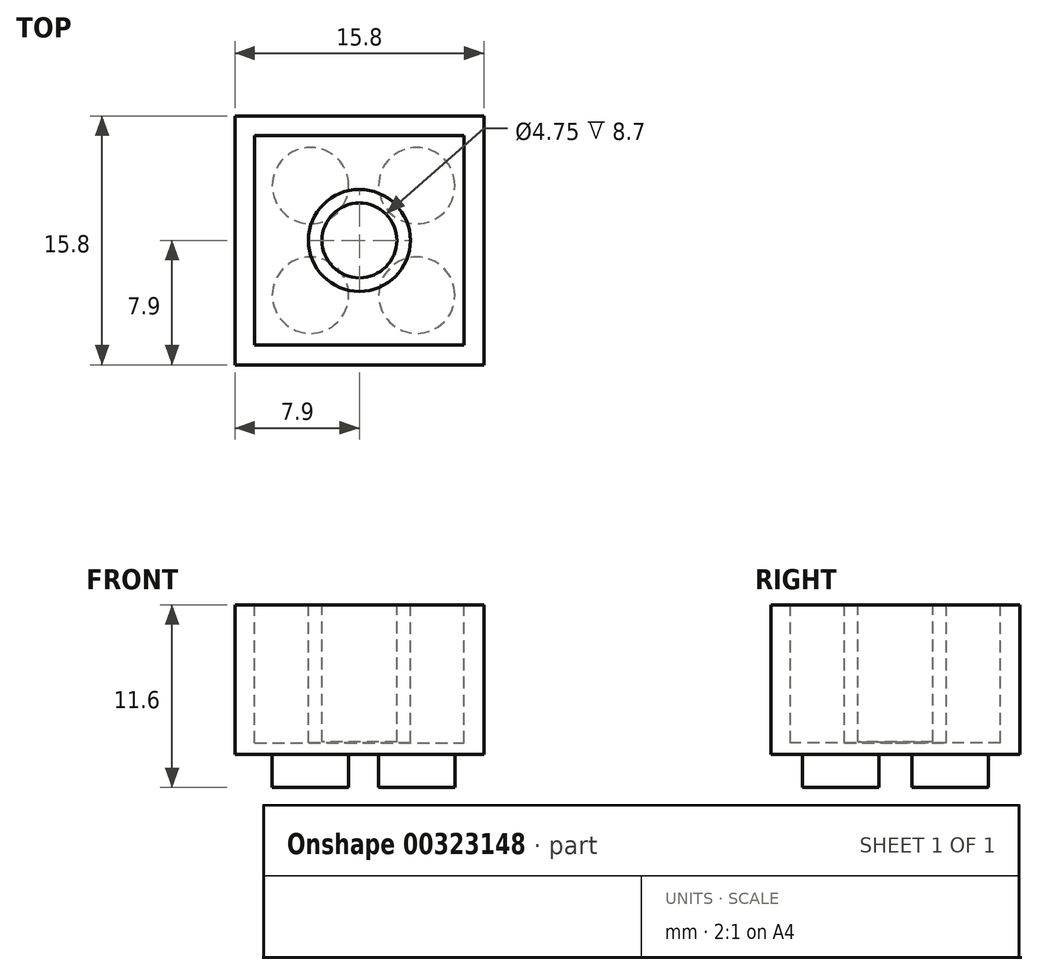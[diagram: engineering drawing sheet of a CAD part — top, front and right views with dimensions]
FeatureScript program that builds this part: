
annotation { "Feature Type Name" : "Feature", "Feature Type Description" : "" }
export const myFeature = defineFeature(function(context is Context, id is Id, definition is map)
    precondition{}
    {
        {
            var Q0;
            Q0=qCreatedBy(makeId("Top.planeOp"),FACE);
            var sketch = newSketch(context, id + "F0", { "sketchPlane" : qUnion([Q0])});
            skLineSegment(sketch, "E0.bottom", {"start": v(7.9, -7.9) * mm, "end": v(-7.9, -7.9) * mm});
            skLineSegment(sketch, "E0.top", {"start": v(7.9, 7.9) * mm, "end": v(-7.9, 7.9) * mm});
            skLineSegment(sketch, "E0.left", {"start": v(7.9, -7.9) * mm, "end": v(7.9, 7.9) * mm});
            skLineSegment(sketch, "E0.right", {"start": v(-7.9, -7.9) * mm, "end": v(-7.9, 7.9) * mm});
            skPoint(sketch, "E0.middle", {"position": v(0, 0) * mm});
            skCircle(sketch, "E1", {"center": v(-3.1, 3.48) * mm, "radius": 2.43 * mm});
            skCircle(sketch, "E2", {"center": v(-3.1, -3.48) * mm, "radius": 2.43 * mm});
            skCircle(sketch, "E3", {"center": v(3.64, -3.48) * mm, "radius": 2.43 * mm});
            skCircle(sketch, "E4", {"center": v(3.64, 3.48) * mm, "radius": 2.43 * mm});
            skSolve(sketch);
        }
        {
            var Q0;
            Q0=makeQuery(id+"F0.imprint","IMPRINT",FACE,{"disambiguationData":[TD([[makeQuery(id+"F0.imprint","IMPRINT",EDGE,{"derivedFrom":sQuery(id+"F0.wireOp",EDGE,"E0.bottom")}),-1.0]])]});
            var Q1;
            Q1=makeQuery(id+"F0.imprint","IMPRINT",FACE,{"disambiguationData":[TD([[makeQuery(id+"F0.imprint","IMPRINT",EDGE,{"derivedFrom":sQuery(id+"F0.wireOp",EDGE,"4mF0htgy-tboj-X3VI-CUVx-4Nb7YP2AiGV2")}),1.0]])]});
            var Q2;
            Q2=makeQuery(id+"F0.imprint","IMPRINT",FACE,{"disambiguationData":[TD([[makeQuery(id+"F0.imprint","IMPRINT",EDGE,{"derivedFrom":sQuery(id+"F0.wireOp",EDGE,"E3")}),1.0]])]});
            var Q3;
            Q3=makeQuery(id+"F0.imprint","IMPRINT",FACE,{"disambiguationData":[TD([[makeQuery(id+"F0.imprint","IMPRINT",EDGE,{"derivedFrom":sQuery(id+"F0.wireOp",EDGE,"E2")}),1.0]])]});
            var Q4;
            Q4=makeQuery(id+"F0.imprint","IMPRINT",FACE,{"disambiguationData":[TD([[makeQuery(id+"F0.imprint","IMPRINT",EDGE,{"derivedFrom":sQuery(id+"F0.wireOp",EDGE,"E1")}),1.0]])]});
            var Q5;
            Q5=makeQuery(id+"F0.imprint","IMPRINT",FACE,{"disambiguationData":[TD([[makeQuery(id+"F0.imprint","IMPRINT",EDGE,{"derivedFrom":sQuery(id+"F0.wireOp",EDGE,"E4")}),1.0]])]});
            extrude(context, id + "F1", {"entities" : qUnion([Q0, Q1, Q2, Q3, Q4, Q5]), "depth" : 9.5 * mm});
        }
        {
            var Q0;
            Q0=makeQuery(id+"F0.imprint","IMPRINT",FACE,{"disambiguationData":[TD([[makeQuery(id+"F0.imprint","IMPRINT",EDGE,{"derivedFrom":sQuery(id+"F0.wireOp",EDGE,"E4")}),1.0]])]});
            var Q1;
            Q1=makeQuery(id+"F0.imprint","IMPRINT",FACE,{"disambiguationData":[TD([[makeQuery(id+"F0.imprint","IMPRINT",EDGE,{"derivedFrom":sQuery(id+"F0.wireOp",EDGE,"E1")}),1.0]])]});
            var Q2;
            Q2=makeQuery(id+"F0.imprint","IMPRINT",FACE,{"disambiguationData":[TD([[makeQuery(id+"F0.imprint","IMPRINT",EDGE,{"derivedFrom":sQuery(id+"F0.wireOp",EDGE,"E2")}),1.0]])]});
            var Q3;
            Q3=makeQuery(id+"F0.imprint","IMPRINT",FACE,{"disambiguationData":[TD([[makeQuery(id+"F0.imprint","IMPRINT",EDGE,{"derivedFrom":sQuery(id+"F0.wireOp",EDGE,"E3")}),1.0]])]});
            extrude(context, id + "F2", {"entities" : qUnion([Q0, Q1, Q2, Q3]), "operationType" : NewBodyOperationType.ADD, "oppositeDirection" : true, "depth" : 2.1 * mm});
        }
        {
            var Q0;
            Q0=makeQuery(id+"F1.opExtrude","CAP_FACE",FACE,{"disambiguationData":[OSD([sQuery(id+"F0.wireOp",EDGE,"E0.bottom"),sQuery(id+"F0.wireOp",EDGE,"E0.top"),sQuery(id+"F0.wireOp",EDGE,"E0.left"),sQuery(id+"F0.wireOp",EDGE,"E0.right")])],"isStart":false});
            var sketch = newSketch(context, id + "F3", { "sketchPlane" : qUnion([Q0])});
            skCircle(sketch, "E5", {"center": v(0, 0) * mm, "radius": 3.24 * mm});
            skLineSegment(sketch, "E6.bottom", {"start": v(-7.9, 7.9) * mm, "end": v(-6.66, 7.9) * mm});
            skLineSegment(sketch, "E6.top", {"start": v(-7.9, -7.9) * mm, "end": v(-6.66, -7.9) * mm});
            skLineSegment(sketch, "E6.left", {"start": v(-7.9, 7.9) * mm, "end": v(-7.9, -7.9) * mm});
            skLineSegment(sketch, "E6.right", {"start": v(-6.66, 7.9) * mm, "end": v(-6.66, -7.9) * mm});
            skLineSegment(sketch, "E7.bottom", {"start": v(-7.9, -7.9) * mm, "end": v(7.9, -7.9) * mm});
            skLineSegment(sketch, "E7.top", {"start": v(-7.9, -6.66) * mm, "end": v(7.9, -6.66) * mm});
            skLineSegment(sketch, "E7.left", {"start": v(-7.9, -7.9) * mm, "end": v(-7.9, -6.66) * mm});
            skLineSegment(sketch, "E7.right", {"start": v(7.9, -7.9) * mm, "end": v(7.9, -6.66) * mm});
            skLineSegment(sketch, "E8.bottom", {"start": v(-7.9, 7.9) * mm, "end": v(7.9, 7.9) * mm});
            skLineSegment(sketch, "E8.top", {"start": v(-7.9, 6.66) * mm, "end": v(7.9, 6.66) * mm});
            skLineSegment(sketch, "E8.left", {"start": v(-7.9, 7.9) * mm, "end": v(-7.9, 6.66) * mm});
            skLineSegment(sketch, "E8.right", {"start": v(7.9, 7.9) * mm, "end": v(7.9, 6.66) * mm});
            skLineSegment(sketch, "E9.bottom", {"start": v(7.9, 7.9) * mm, "end": v(6.66, 7.9) * mm});
            skLineSegment(sketch, "E9.top", {"start": v(7.9, -7.9) * mm, "end": v(6.66, -7.9) * mm});
            skLineSegment(sketch, "E9.left", {"start": v(7.9, 7.9) * mm, "end": v(7.9, -7.9) * mm});
            skLineSegment(sketch, "E9.right", {"start": v(6.66, 7.9) * mm, "end": v(6.66, -7.9) * mm});
            skSolve(sketch);
        }
        {
            var Q0;
            Q0=makeQuery(id+"F3.imprint","IMPRINT",FACE,{"disambiguationData":[TD([[makeQuery(id+"F3.imprint","IMPRINT",EDGE,{"derivedFrom":sQuery(id+"F3.wireOp",EDGE,"E5")}),-1.0]])]});
            extrude(context, id + "F4", {"entities" : qUnion([Q0]), "operationType" : NewBodyOperationType.REMOVE, "oppositeDirection" : true, "depth" : 8.76 * mm});
        }
        {
            var Q0;
            Q0=makeQuery(id+"F4.boolean.opBoolean","SPLIT",FACE,{"disambiguationData":[TD([makeQuery(id+"F4.opExtrude","SWEPT_FACE",FACE,{"disambiguationData":[OSD([sQuery(id+"F3.wireOp",EDGE,"E5")])]})])],"derivedFrom":makeQuery(id+"F1.opExtrude","CAP_FACE",FACE,{"disambiguationData":[OSD([sQuery(id+"F0.wireOp",EDGE,"E0.bottom"),sQuery(id+"F0.wireOp",EDGE,"E0.top"),sQuery(id+"F0.wireOp",EDGE,"E0.left"),sQuery(id+"F0.wireOp",EDGE,"E0.right")])],"isStart":false})});
            var sketch = newSketch(context, id + "F5", { "sketchPlane" : qUnion([Q0])});
            skCircle(sketch, "E10", {"center": v(0, 0) * mm, "radius": 2.38 * mm});
            skSolve(sketch);
        }
        {
            var Q0;
            Q0=makeQuery(id+"F5.imprint","IMPRINT",FACE,{"disambiguationData":[TD([[makeQuery(id+"F5.imprint","IMPRINT",EDGE,{"derivedFrom":sQuery(id+"F5.wireOp",EDGE,"E10")}),1.0]])]});
            extrude(context, id + "F6", {"entities" : qUnion([Q0]), "operationType" : NewBodyOperationType.REMOVE, "oppositeDirection" : true, "depth" : 8.7 * mm});
        }
    });
